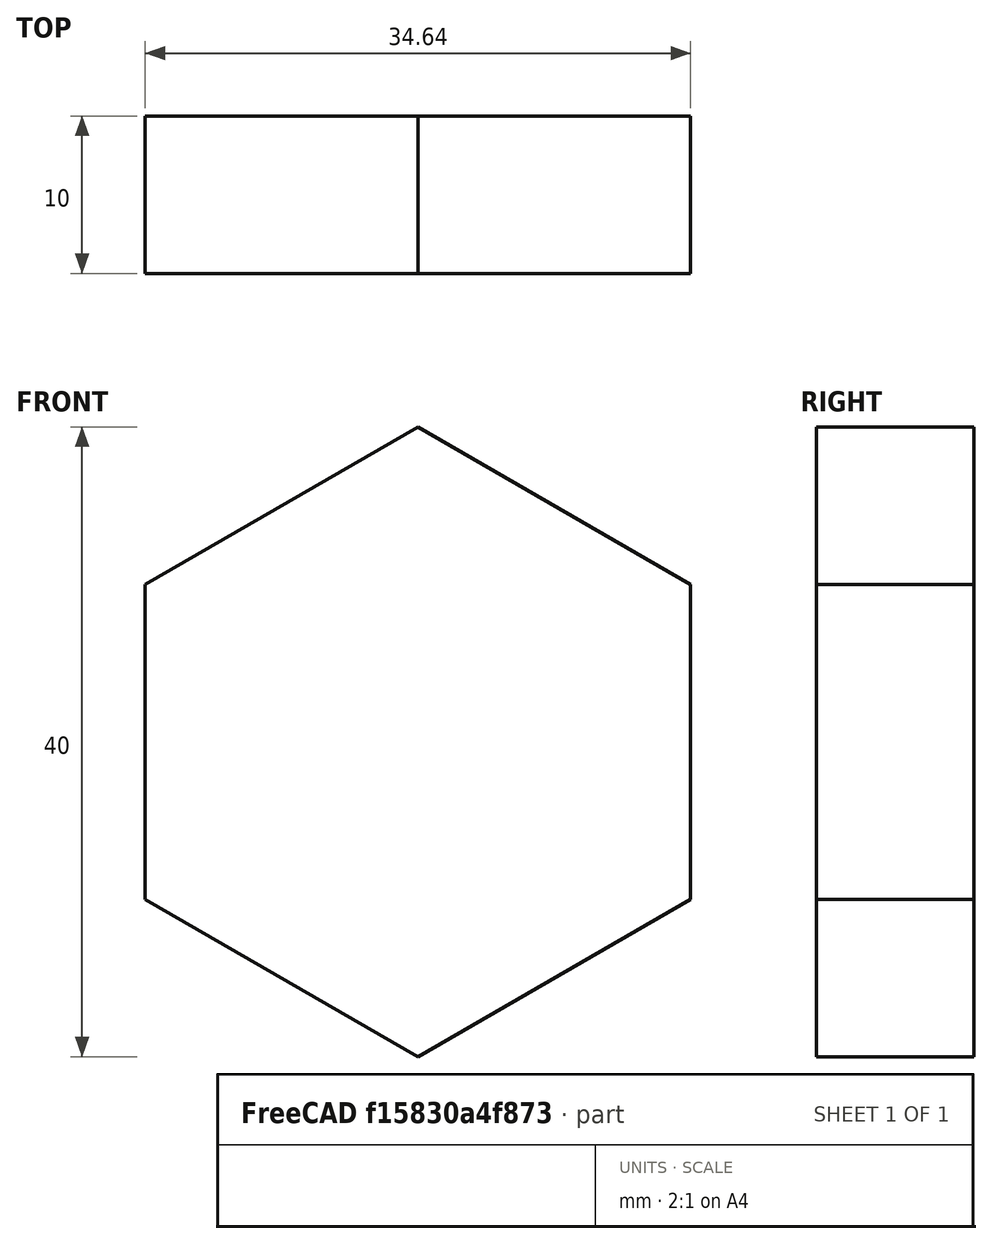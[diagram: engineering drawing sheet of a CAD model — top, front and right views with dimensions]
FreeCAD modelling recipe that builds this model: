
FCSTD DOCUMENT  (FreeCAD 2023.521R14555 (Git shallow))
Label: Hex
License: All rights reserved
objects: Sketcher::SketchObject×1, PartDesign::Pad×1, PartDesign::Body×1, App::Link×1, PartDesign::CoordinateSystem×1, App::Part×1
note: 7 computed .brp shape members not serialized (recipe doc carries the construction recipe); baked Part::Feature solids carry a one-line shape summary decoded from their .brp
EXTERNAL_REF file=Main_board.FCStd obj=Spreadsheet

FEATURE [Sketcher::SketchObject] Sketch
  ArcFitTolerance = 1e-06
  AttachmentSupport = -> [XZ_Plane001]
  ExternalBSplineMaxDegree = 5
  ExternalBSplineTolerance = 0.0001
  FullyConstrained = true
  InternalTolerance = 1e-06
  InvalidShape = false
  MakeInternals = false
  MapMode = 5
  Placement = pos=(0,0,0) rot=(1,0,0;1.5708rad)
  Support = -> [XZ_Plane001]
  TreeRank = 23
  ValidateShape = false
  expr: Constraints[18] = <<dims>>.PS
  sketch-geometry (7):
    g0: LineSegment StartX=-17.3205 StartY=10 StartZ=0 EndX=-17.3205 EndY=-10 EndZ=0
    g1: LineSegment StartX=-17.3205 StartY=-10 StartZ=0 EndX=3.6e-15 EndY=-20 EndZ=0
    g2: LineSegment StartX=2.1e-15 StartY=-20 StartZ=0 EndX=17.3205 EndY=-10 EndZ=0
    g3: LineSegment StartX=17.3205 StartY=-10 StartZ=0 EndX=17.3205 EndY=10 EndZ=0
    g4: LineSegment StartX=17.3205 StartY=10 StartZ=0 EndX=0 EndY=20 EndZ=0
    g5: LineSegment StartX=2e-16 StartY=20 StartZ=0 EndX=-17.3205 EndY=10 EndZ=0
    g6: Circle [constr] CenterX=0 CenterY=0 CenterZ=0 NormalX=0 NormalY=0 NormalZ=1 AngleXU=0 Radius=20
  constraints (16):
    c: Coincident(g0,g1)
    c: Coincident(g1,g2)
    c: Coincident(g2,g3)
    c: Coincident(g3,g4)
    c: Coincident(g4,g5)
    c: Coincident(g5,g0)
    c: Equal(g0, g1-g5) x5
    c: PointOnObject(g0,g6)
    c: PointOnObject(g1,g6)
    c: PointOnObject(g2,g6)
    c: PointOnObject(g3,g6)
    c: PointOnObject(g4,g6)
    c: PointOnObject(g5,g6)
    c: Coincident(g6,g-1)
    c: Diameter(g6) = 40
    c: Vertical(g3)
FEATURE [PartDesign::Pad] Pad
  AddSubType = 0
  AlongSketchNormal = false
  AutoTaperInnerAngle = true
  CheckUpToFaceLimits = true
  ClaimChildren = false
  Direction = (0,-1,-2e-16)
  Fit = 0
  FitJoin = 0
  InnerFit = 0
  InnerFitJoin = 0
  InvalidShape = false
  Length = 10
  Length2 = 10
  Linearize = true
  NewSolid = false
  Profile = -> Sketch
  ReferenceAxis = -> Sketch [N_Axis]
  Suppress = false
  TaperInnerAngle = 0
  TaperInnerAngleRev = 0
  TreeRank = 24
  Type = 0
  ValidateShape = true
  _ProfileBasedVersion = 1
FEATURE [PartDesign::Body] Body
  AutoGroupSolids = false
  ClaimAllChildren = false
  ExportMode = 0
  Group = -> [Sketch,Pad]
  InvalidShape = false
  Origin = -> Origin001
  Tip = -> Pad
  TreeRank = 22
  ValidateShape = false
  _ExportChildren = -> [Pad]
  _GroupVersion = 1
FEATURE [App::Link] Link  label="dims"
  AutoLinkLabel = true
  AutoPlacement = true
  LinkedObject = -> <external Main_board.FCStd>#Spreadsheet
  SyncGroupVisibility = false
  TreeRank = 26
  _LinkVersion = 1
FEATURE [PartDesign::CoordinateSystem] Local_CS001
  AttacherType = Attacher::AttachEngine3D
  AttachmentSupport = -> [XZ_Plane]
  InvalidShape = false
  MapMode = 5
  Placement = pos=(0,0,0) rot=(0,0.707107,0.707107;3.14159rad)
  Support = -> [XZ_Plane]
  TreeRank = 30
  ValidateShape = false
FEATURE [App::Part] Hex
  ClaimAllChildren = false
  ExportMode = 1
  Group = -> [Body,Local_CS001]
  Origin = -> Origin
  TreeRank = 11
  _ExportChildren = -> [Body,Local_CS001]
  _GroupVersion = 1

RESOLVED EXTERNAL PARTS (link-assembly join: the EXTERNAL_REF files above that resolve inside this repo's crawl, each included once):
---- part Main_board.FCStd = doc fcstd_18a85a5c1fb4 ----
FCSTD DOCUMENT  (FreeCAD 2023.521R14555 (Git shallow))
Label: Main_board
License: All rights reserved
objects: PartDesign::CoordinateSystem×5, Sketcher::SketchObject×2, PartDesign::Pad×1, Spreadsheet::Sheet×1, PartDesign::Body×1, App::Part×1
note: 13 computed .brp shape members not serialized (recipe doc carries the construction recipe); baked Part::Feature solids carry a one-line shape summary decoded from their .brp

FEATURE [Sketcher::SketchObject] Sketch
  ArcFitTolerance = 1e-06
  AttachmentSupport = -> [XZ_Plane]
  ExternalBSplineMaxDegree = 5
  ExternalBSplineTolerance = 0.0001
  FullyConstrained = true
  InternalTolerance = 1e-06
  InvalidShape = false
  MakeInternals = false
  MapMode = 5
  Placement = pos=(0,0,0) rot=(1,0,0;1.5708rad)
  Support = -> [XZ_Plane]
  TreeRank = 11
  ValidateShape = false
  expr: Constraints[48] = <<dims>>.HS
  sketch-geometry (31):
    g0: LineSegment StartX=-40 StartY=19 StartZ=0 EndX=-21.8135 EndY=50.5 EndZ=0
    g1: LineSegment StartX=-21.8135 StartY=50.5 StartZ=0 EndX=-58.1865 EndY=50.5 EndZ=0
    g2: LineSegment StartX=-58.1865 StartY=50.5 StartZ=0 EndX=-40 EndY=19 EndZ=0
    g3: Circle [constr] CenterX=-40 CenterY=40 CenterZ=0 NormalX=0 NormalY=0 NormalZ=1 AngleXU=0 Radius=21
    g4: LineSegment StartX=40 StartY=-19 StartZ=0 EndX=21.8135 EndY=-50.5 EndZ=0
    g5: LineSegment StartX=21.8135 StartY=-50.5 StartZ=0 EndX=58.1865 EndY=-50.5 EndZ=0
    g6: LineSegment StartX=58.1865 StartY=-50.5 StartZ=0 EndX=40 EndY=-19 EndZ=0
    g7: Circle [constr] CenterX=40 CenterY=-40 CenterZ=0 NormalX=0 NormalY=0 NormalZ=1 AngleXU=0 Radius=21
    g8: LineSegment StartX=27.6565 StartY=23.0106 StartZ=0 EndX=52.3435 EndY=23.0106 EndZ=0
    g9: LineSegment StartX=52.3435 StartY=23.0106 StartZ=0 EndX=59.9722 EndY=46.4894 EndZ=0
    g10: LineSegment StartX=59.9722 StartY=46.4894 StartZ=0 EndX=40 EndY=61 EndZ=0
    g11: LineSegment StartX=40 StartY=61 StartZ=0 EndX=20.0278 EndY=46.4894 EndZ=0
    g12: LineSegment StartX=20.0278 StartY=46.4894 StartZ=0 EndX=27.6565 EndY=23.0106 EndZ=0
    g13: Circle [constr] CenterX=40 CenterY=40 CenterZ=0 NormalX=0 NormalY=0 NormalZ=1 AngleXU=0 Radius=21
    g14: LineSegment StartX=-21.8135 StartY=-29.5 StartZ=0 EndX=-40 EndY=-19 EndZ=0
    g15: LineSegment StartX=-40 StartY=-19 StartZ=0 EndX=-58.1865 EndY=-29.5 EndZ=0
    g16: LineSegment StartX=-58.1865 StartY=-29.5 StartZ=0 EndX=-58.1865 EndY=-50.5 EndZ=0
    g17: LineSegment StartX=-58.1865 StartY=-50.5 StartZ=0 EndX=-40 EndY=-61 EndZ=0
    g18: LineSegment StartX=-40 StartY=-61 StartZ=0 EndX=-21.8135 EndY=-50.5 EndZ=0
    g19: LineSegment StartX=-21.8135 StartY=-50.5 StartZ=0 EndX=-21.8135 EndY=-29.5 EndZ=0
    g20: Circle [constr] CenterX=-40 CenterY=-40 CenterZ=0 NormalX=0 NormalY=0 NormalZ=1 AngleXU=0 Radius=21
    g21: Circle CenterX=0 CenterY=0 CenterZ=0 NormalX=0 NormalY=0 NormalZ=1 AngleXU=0 Radius=21
    g22: LineSegment [constr] StartX=-40 StartY=40 StartZ=0 EndX=40 EndY=40 EndZ=0
    g23: LineSegment [constr] StartX=40 StartY=40 StartZ=0 EndX=40 EndY=-40 EndZ=0
    g24: LineSegment [constr] StartX=40 StartY=-40 StartZ=0 EndX=-40 EndY=-40 EndZ=0
    g25: LineSegment [constr] StartX=-40 StartY=-40 StartZ=0 EndX=-40 EndY=40 EndZ=0
    g26: LineSegment StartX=-70 StartY=-70 StartZ=0 EndX=-70 EndY=70 EndZ=0
    g27: LineSegment StartX=-70 StartY=70 StartZ=0 EndX=70 EndY=70 EndZ=0
    g28: LineSegment StartX=70 StartY=70 StartZ=0 EndX=70 EndY=-70 EndZ=0
    g29: LineSegment StartX=70 StartY=-70 StartZ=0 EndX=-70 EndY=-70 EndZ=0
    g30: GeomPoint [constr] X=0 Y=0 Z=0
  constraints (77):
    c: Coincident(g0,g1)
    c: Coincident(g1,g2)
    c: Coincident(g2,g0)
    c: Equal(g0,g1)
    c: Equal(g0,g2)
    c: PointOnObject(g0,g3)
    c: PointOnObject(g1,g3)
    c: PointOnObject(g2,g3)
    c: Coincident(g4,g5)
    c: Coincident(g5,g6)
    c: Coincident(g6,g4)
    c: Equal(g4,g5)
    c: Equal(g4,g6)
    c: PointOnObject(g4,g7)
    c: PointOnObject(g5,g7)
    c: PointOnObject(g6,g7)
    c: Coincident(g8,g9)
    c: Coincident(g9,g10)
    c: Coincident(g10,g11)
    c: Coincident(g11,g12)
    c: Coincident(g12,g8)
    c: Equal(g8, g9-g12) x4
    c: PointOnObject(g8,g13)
    c: PointOnObject(g9,g13)
    c: PointOnObject(g10,g13)
    c: PointOnObject(g11,g13)
    c: PointOnObject(g12,g13)
    c: Coincident(g14,g15)
    c: Coincident(g15,g16)
    c: Coincident(g16,g17)
    c: Coincident(g17,g18)
    c: Coincident(g18,g19)
    c: Coincident(g19,g14)
    c: Equal(g14, g15-g19) x5
    c: PointOnObject(g14,g20)
    c: PointOnObject(g15,g20)
    c: PointOnObject(g16,g20)
    c: PointOnObject(g17,g20)
    c: PointOnObject(g18,g20)
    c: PointOnObject(g19,g20)
    c: Coincident(g21,g-1)
    c: Diameter(g13) = 42
    c: Horizontal(g8)
    c: Equal(g13,g7)
    c: Equal(g7,g20)
    c: Equal(g20,g3)
    c: Vertical(g19)
    c: Horizontal(g5)
    c: Horizontal(g1)
    c: Coincident(g22,g23)
    c: Coincident(g23,g24)
    c: Coincident(g24,g25)
    c: Coincident(g25,g22)
    c: Horizontal(g22)
    c: Horizontal(g24)
    c: Vertical(g23)
    c: Vertical(g25)
    c: Coincident(g22,g3)
    c: Coincident(g23,g7)
    c: Coincident(g22,g13)
    c: Coincident(g24,g20)
    c: Symmetric(g24,g22,g21)
    c: Equal(g23,g24)
    c: DistanceY(g23,g23) = 80
    c: Coincident(g26,g27)
    c: Coincident(g27,g28)
    c: Coincident(g28,g29)
    c: Coincident(g29,g26)
    c: Horizontal(g27)
    c: Horizontal(g29)
    c: Vertical(g26)
    c: Vertical(g28)
    c: Symmetric(g27,g26,g30)
    c: Coincident(g30,g21)
    c: Equal(g28,g29)
    c: DistanceY(g28,g28) = 140
    c: Equal(g21,g13)
FEATURE [PartDesign::Pad] Pad
  AddSubType = 0
  AlongSketchNormal = false
  AutoTaperInnerAngle = true
  CheckUpToFaceLimits = true
  ClaimChildren = false
  Direction = (0,-1,-2e-16)
  Fit = 0
  FitJoin = 0
  InnerFit = 0
  InnerFitJoin = 0
  InvalidShape = false
  Length = 4
  Length2 = 10
  Linearize = true
  NewSolid = false
  Profile = -> Sketch
  ReferenceAxis = -> Sketch [N_Axis]
  Suppress = false
  TaperInnerAngle = 0
  TaperInnerAngleRev = 0
  TreeRank = 12
  Type = 0
  ValidateShape = true
  _ProfileBasedVersion = 1
FEATURE [PartDesign::CoordinateSystem] Local_CS  label="Triangle0"
  AttacherType = Attacher::AttachEngine3D
  AttachmentSupport = -> [Pad]
  InvalidShape = false
  MapMode = 13
  Placement = pos=(-40,-4,40) rot=(1,0,0;1.5708rad)
  Support = -> [Pad]
  TreeRank = 16
  ValidateShape = false
FEATURE [PartDesign::CoordinateSystem] Local_CS002  label="Triangle1"
  AttacherType = Attacher::AttachEngine3D
  AttachmentOffset = pos=(0,0,0) rot=(0,0,1;3.14159rad)
  AttachmentSupport = -> [Pad]
  InvalidShape = false
  MapMode = 13
  Placement = pos=(40,-4,-40) rot=(0,-0.707107,0.707107;3.14159rad)
  Support = -> [Pad]
  TreeRank = 21
  ValidateShape = false
FEATURE [PartDesign::CoordinateSystem] Local_CS003  label="Circle"
  AttacherType = Attacher::AttachEngine3D
  AttachmentSupport = -> [Pad]
  InvalidShape = false
  MapMode = 11
  Placement = pos=(0,-4,-9e-16) rot=(0.57735,-0.57735,0.57735;2.0944rad)
  Support = -> [Pad]
  TreeRank = 22
  ValidateShape = false
FEATURE [Spreadsheet::Sheet] Spreadsheet  label="dims"
  PythonMode = false
  ShowCells = 0
  TreeRank = 25
  cells = A1=Part SIze; B1(PS)==40mm; A2=Gap; B2==2mm; A3=Hole Size; B3(HS)==B1 + B2
FEATURE [Sketcher::SketchObject] Sketch001
  ArcFitTolerance = 1e-06
  AttachmentSupport = -> [Pad]
  ExternalBSplineMaxDegree = 5
  ExternalBSplineTolerance = 0.0001
  ExternalGeometry = -> [Pad]
  FullyConstrained = true
  InternalTolerance = 1e-06
  InvalidShape = false
  MakeInternals = false
  MapMode = 5
  Placement = pos=(0,-4,-9e-16) rot=(1,0,0;1.5708rad)
  Support = -> [Pad]
  TreeRank = 26
  ValidateShape = false
  sketch-geometry (2):
    g0: Circle CenterX=40 CenterY=40 CenterZ=0 NormalX=0 NormalY=0 NormalZ=1 AngleXU=0 Radius=21
    g1: Circle CenterX=-40 CenterY=-40 CenterZ=0 NormalX=0 NormalY=0 NormalZ=1 AngleXU=0 Radius=21
  constraints (6):
    c: PointOnObject(g-4,g0)
    c: PointOnObject(g-3,g0)
    c: PointOnObject(g-3,g0)
    c: PointOnObject(g-5,g1)
    c: PointOnObject(g-6,g1)
    c: PointOnObject(g-6,g1)
FEATURE [PartDesign::Body] Body
  AutoGroupSolids = false
  ClaimAllChildren = false
  ExportMode = 0
  Group = -> [Sketch,Pad,Sketch001]
  InvalidShape = false
  Origin = -> Origin
  Tip = -> Pad
  TreeRank = 10
  ValidateShape = false
  _ExportChildren = -> [Pad,Sketch001]
  _GroupVersion = 1
FEATURE [PartDesign::CoordinateSystem] Local_CS004  label="Penta"
  AttacherType = Attacher::AttachEngine3D
  AttachmentSupport = -> [Sketch001]
  InvalidShape = false
  MapMode = 11
  Placement = pos=(40,-4,40) rot=(-0.57735,0.57735,-0.57735;4.18879rad)
  Support = -> [Sketch001]
  TreeRank = 23
  ValidateShape = false
FEATURE [PartDesign::CoordinateSystem] Local_CS005  label="Hex"
  AttacherType = Attacher::AttachEngine3D
  AttachmentSupport = -> [Sketch001]
  InvalidShape = false
  MapMode = 11
  Placement = pos=(-40,-4,-40) rot=(-0.57735,0.57735,-0.57735;4.18879rad)
  Support = -> [Sketch001]
  TreeRank = 24
  ValidateShape = false
FEATURE [App::Part] Part
  ClaimAllChildren = false
  ExportMode = 1
  Group = -> [Body,Local_CS,Local_CS002,Local_CS003,Local_CS004,Local_CS005]
  Origin = -> Origin001
  TreeRank = 15
  _ExportChildren = -> [Body,Local_CS,Local_CS002,Local_CS003,Local_CS004,Local_CS005]
  _GroupVersion = 1
